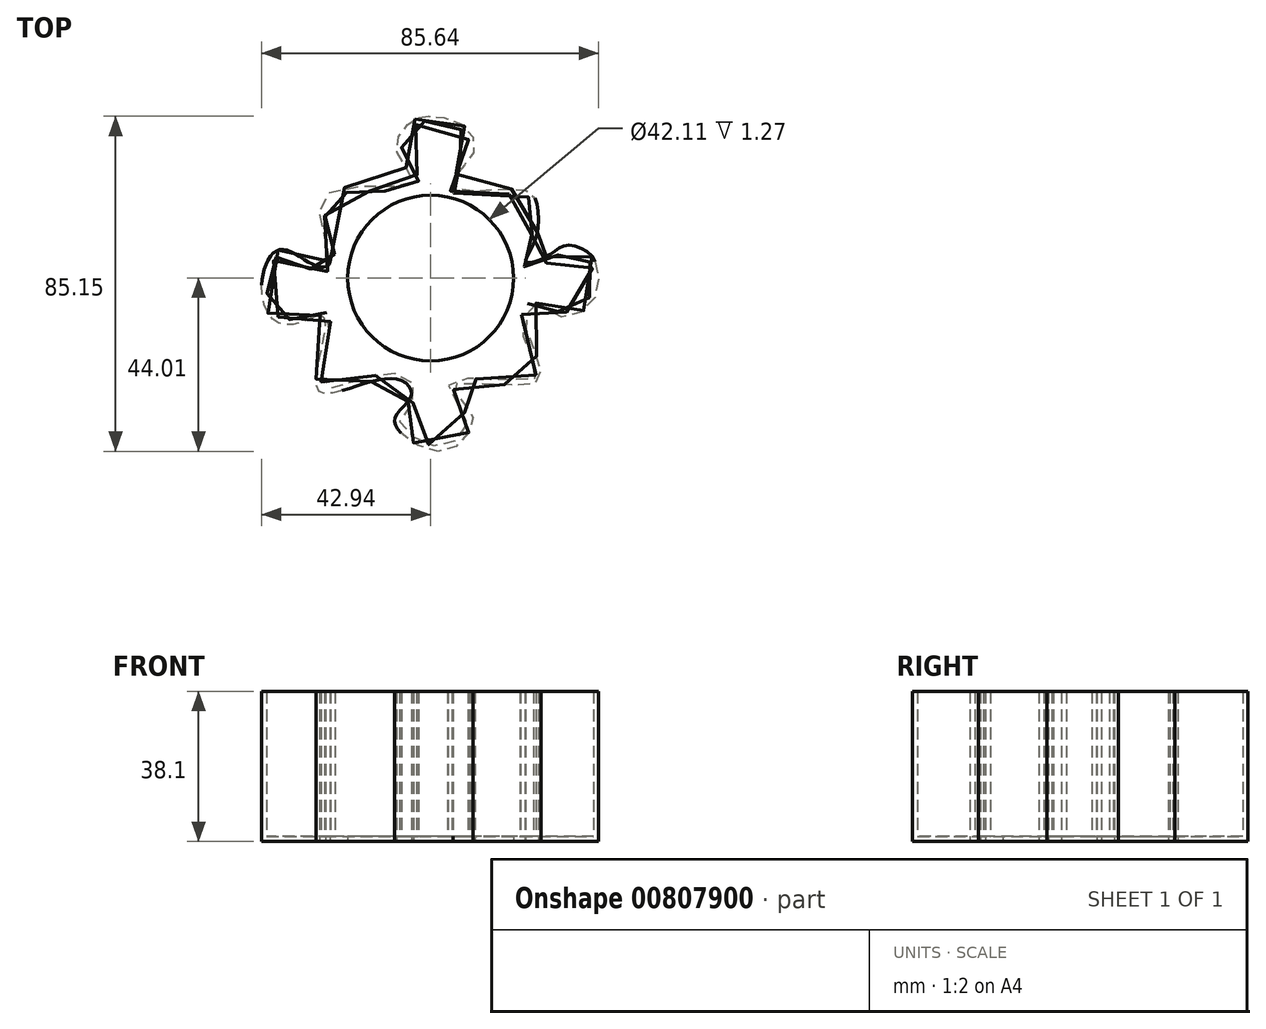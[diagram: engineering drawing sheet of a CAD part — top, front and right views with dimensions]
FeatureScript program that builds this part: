
annotation { "Feature Type Name" : "Feature", "Feature Type Description" : "" }
export const myFeature = defineFeature(function(context is Context, id is Id, definition is map)
    precondition{}
    {
        {
            var Q0;
            Q0=qCreatedBy(makeId("Top.planeOp"),FACE);
            var sketch = newSketch(context, id + "F0", { "sketchPlane" : qUnion([Q0])});
            skFitSpline(sketch, "E0", {"points": [v(-25.56, 4.15) * mm, v(-27.13, 20.74) * mm, v(-4.58, 24.19) * mm, v(-8.03, 30.76) * mm, v(-7.4, 37.34) * mm, v(-3.02, 40.78) * mm, v(0, 41.1) * mm, v(8.25, 38.9) * mm, v(11.07, 32.33) * mm, v(6.69, 26.7) * mm, v(6.06, 22.94) * mm, v(22.66, 22.62) * mm, v(26.73, 19.8) * mm, v(26.42, 9.16) * mm, v(24.22, 4.15) * mm, v(29.55, 5.4) * mm, v(33.93, 8.22) * mm, v(40.2, 6.34) * mm, v(42.7, 0) * mm, v(39.57, -7.75) * mm, v(31.11, -9.31) * mm, v(27.67, -6.18) * mm, v(24.22, -9.63) * mm, v(25.48, -16.2) * mm, v(27.67, -25.91) * mm, v(20.78, -27.16) * mm, v(10.45, -26.85) * mm, v(5.75, -27.48) * mm, v(8.88, -32.49) * mm, v(10.76, -35.62) * mm, v(7.63, -41.88) * mm, v(0, -43.76) * mm, v(-8.34, -38.44) * mm, v(-8.65, -34.68) * mm, v(-4.9, -29.67) * mm, v(-7.71, -25.91) * mm, v(-18.99, -27.48) * mm, v(-28.38, -28.73) * mm, v(-27.44, -16.83) * mm, v(-27.44, -9.63) * mm, v(-33.7, -11.5) * mm, v(-40.28, -10.25) * mm, v(-42.78, 0) * mm, v(-38.09, 7.28) * mm, v(-29.32, 3.21) * mm, v(-25.56, 4.15) * mm]});
            skSolve(sketch);
        }
        {
            var Q0;
            Q0=makeQuery(id+"F0.imprint","IMPRINT",FACE,{"disambiguationData":[TD([[makeQuery(id+"F0.imprint","IMPRINT",EDGE,{"derivedFrom":sQuery(id+"F0.wireOp",EDGE,"E0")}),-1.0]])]});
            extrude(context, id + "F1", {"entities" : qUnion([Q0]), "depth" : 38.1 * mm, "offsetDistance" : 25.4 * mm});
        }
        {
            var Q0;
            Q0=makeQuery(id+"F1.opExtrude","CAP_FACE",FACE,{"disambiguationData":[OSD([sQuery(id+"F0.wireOp",EDGE,"E0")])],"isStart":false});
            shell(context, id + "F2", {"entities" : qUnion([Q0]), "thickness" : 1.27 * mm});
        }
        {
            var Q0;
            Q0=makeQuery(id+"F1.opExtrude","CAP_FACE",FACE,{"disambiguationData":[OSD([sQuery(id+"F0.wireOp",EDGE,"E0")])],"isStart":true});
            var sketch = newSketch(context, id + "F3", { "sketchPlane" : qUnion([Q0])});
            skCircle(sketch, "E1", {"center": v(0, 0) * mm, "radius": 21.05 * mm});
            skSolve(sketch);
        }
        {
            var Q0;
            Q0 = qSketchRegion(id + "F3", true);
            extrude(context, id + "F4", {"entities" : qUnion([Q0]), "operationType" : NewBodyOperationType.REMOVE, "oppositeDirection" : true, "depth" : 25.4 * mm, "offsetDistance" : 25.4 * mm});
        }
    });
